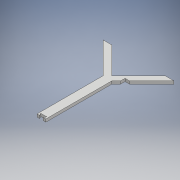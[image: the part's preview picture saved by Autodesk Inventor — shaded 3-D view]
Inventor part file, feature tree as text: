
AUTODESK INVENTOR PART (.ipt)
format: ipt  version: 2017 (Build 210142000, 142)  size: 116,224 bytes
history: native  units: mm
features: extrude x1
ambient origin geometry x8: Origin, YZ Plane, XZ Plane, XY Plane, X Axis, Y Axis, Z Axis, Center Point
bodies: Solid1 (feature_tree)
feature tree (1):
  extrude  "Extrusion1"  Depth=5.0mm
